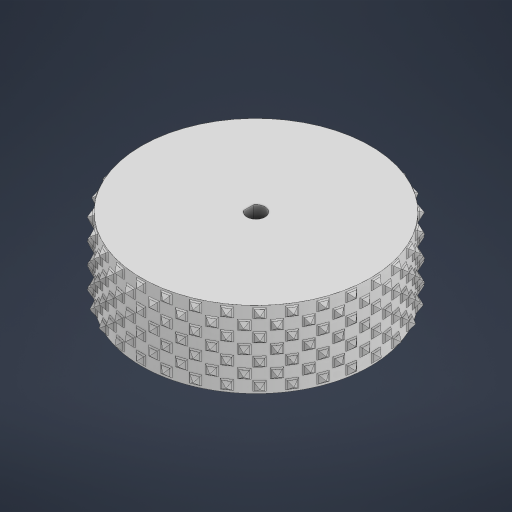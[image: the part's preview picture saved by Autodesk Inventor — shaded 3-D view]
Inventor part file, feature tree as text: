
AUTODESK INVENTOR PART (.ipt)
format: ipt  version: 2024.1 (Build 281209000, 209)  size: 12,331,520 bytes
history: native  units: in
note: dims shown in document units (in); Inventor stores cm internally (conversion verified against a paired STEP export)
features: chamfer x11, extrude x2, pattern_circular x2, sketch x2, plane x1, fillet x1
ambient origin geometry x8: Origin, YZ Plane, XZ Plane, XY Plane, X Axis, Y Axis, Z Axis, Center Point
bodies: Solid1 (feature_tree)
feature tree (19):
  extrude  "Extrusion1"  Depth=0.2362in
  plane  "Work Plane1"
  extrude  "Extrusion2"  Depth=0.125in TaperAngle=0.0deg
  chamfer  "Chamfer18"  Distance=0.125in
  fillet  "Fillet1"  Radius=0.125in
  pattern_circular  "Circular Pattern3"  [2 undecoded]
  chamfer  "Chamfer8"  Distance=0.125in
  chamfer  "Chamfer9"  Distance=0.15in
  chamfer  "Chamfer10"  Distance=0.125in
  chamfer  "Chamfer11"  Distance=0.125in
  chamfer  "Chamfer12"  Distance=0.15in
  chamfer  "Chamfer13"  Distance=0.125in
  chamfer  "Chamfer14"  Distance=0.125in
  chamfer  "Chamfer15"  Distance=0.15in
  chamfer  "Chamfer16"  Distance=0.5in
  chamfer  "Chamfer17"  Distance=0.1in Angle=45.0deg
  pattern_circular  "Circular Pattern2"  Angle=45.0deg  [1 undecoded]
  sketch  "Sketch1"  dims[d0=3.0in d1=0.2362in]
  sketch  "Sketch2"  dims[d2=0.2165in d3=1.0in d4=0.0in d5=0.125in d6=0.125in d7=0.125in d8=0.125in d9=0.15in d10=0.125in d11=0.125in d12=0.15in d16=0.125in d17=0.125in d19=0.15in d20=0.125in d21=0.125in d22=0.125in d23=0.125in d24=0.15in d25=0.125in d26=0.125in d27=0.15in d33=0.065in d34=0.0in d62=0.5in d63=0.1in d64=0.075in d65=45.0deg d66=0.1in d67=0.075in d68=45.0deg d69=0.1in d70=0.075in d71=45.0deg d72=0.1in d73=0.075in d74=45.0deg d75=0.1in d76=0.075in d77=45.0deg d78=0.1in d79=0.075in d80=45.0deg d81=0.1in d82=0.075in d83=45.0deg d84=0.1in d85=0.075in d86=45.0deg d87=0.1in d88=0.075in d89=45.0deg d90=0.1in d91=0.075in d92=45.0deg d93=9.4488in d94=360.0deg d96=0.0625in d97=0.0813in d99=0.1375in d100=0.0813in d101=0.0125in d102=0.0625in d103=0.125in d104=45.0deg d105=12.2047in d106=360.0deg d108=0.125in d107=0.0in]
note: 3 required parameter values undecoded (feature->parameter linkage not recoverable at this tier; creation-order binding heuristic only, values carry confidence <= 0.55)
